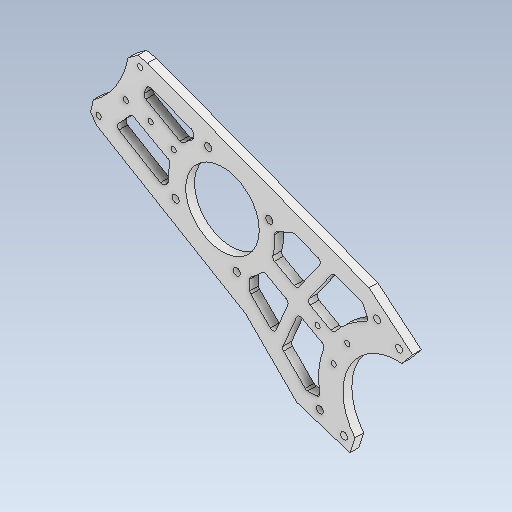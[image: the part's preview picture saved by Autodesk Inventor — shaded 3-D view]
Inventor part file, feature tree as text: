
AUTODESK INVENTOR PART (.ipt)
format: ipt  version: 2020 (Build 240168000, 168)  size: 496,128 bytes
history: native  units: mm
features: reference x14, sketch x11, extrude x10, other x7, thicken_offset x3, projected_geometry x3, chamfer x2, hole x1, fillet x1
ambient origin geometry x8: Origin, YZ Plane, XZ Plane, XY Plane, X Axis, Y Axis, Z Axis, Center Point
bodies: Solid1 (feature_tree)
feature tree (52):
  extrude  "Extrusion1"  Depth=5.0mm
  extrude  "Extrusion2"  Depth=5.0mm TaperAngle=0.0deg
  extrude  "Extrusion3"  Depth=4.0mm
  thicken_offset  "Thicken1"
  extrude  "Extrusion4"  Depth=5.0mm TaperAngle=0.0deg
  extrude  "Extrusion5"  Depth=10.0mm TaperAngle=0.0deg
  extrude  "Extrusion6"  Depth=2.0mm
  hole  "Hole1"  [1 undecoded]
  extrude  "Extrusion7"  Depth=10.0mm TaperAngle=0.0deg
  extrude  "Extrusion9"  Depth=60.0mm
  extrude  "Extrusion10"  Depth=10.0mm
  chamfer  "Chamfer1"  Angle=45.0deg  [1 undecoded]
  extrude  "Extrusion11"  TaperAngle=45.0deg  [1 undecoded]
  thicken_offset  "Thicken2"
  thicken_offset  "Thicken3"
  fillet  "Fillet4"  [1 undecoded]
  chamfer  "Chamfer2"  Angle=45.0deg  [1 undecoded]
  sketch  "Sketch1"  dims[d3=5.0mm d4=0.0mm d5=42.0mm]
  reference  "Reference1"
  reference  "Reference2"
  sketch  "Sketch2"  dims[d6=5.0mm d7=0.0mm d8=5.0mm d9=0.0mm]
  reference  "Reference3"
  sketch  "Sketch3"  dims[d10=4.0mm d11=4.0mm]
  reference  "Reference4"
  reference  "Reference5"
  sketch  "Sketch4"  dims[d13=40.0mm d14=5.0mm d15=0.0mm]
  projected_geometry  "Projected Loop1"
  sketch  "Sketch5"  dims[d16=10.0mm d17=0.0mm d18=10.0mm d19=0.0mm]
  reference  "Reference6"
  reference  "Reference7"
  reference  "Reference8"
  reference  "Reference9"
  sketch  "Sketch6"  dims[d20=3.0mm d21=6.0mm d22=4.0mm d23=2.0mm d24=90.0deg d25=8.0mm d26=0.0mm d27=28.0mm]
  projected_geometry  "Projected Loop2"
  sketch  "Sketch7"  dims[d28=18.675023mm d29=4.1mm]
  reference  "Reference10"
  reference  "Reference11"
  reference  "Reference12"
  reference  "Reference13"
  reference  "Reference14"
  sketch  "Sketch8"  dims[d30=40.0mm d32=360.0deg d34=10.0mm d35=0.0mm]
  sketch  "Sketch9"  dims[d36=90.0mm d37=60.0mm]
  sketch  "Sketch10"  dims[d38=14.0mm d39=10.0mm]
  projected_geometry  "Projected Loop3"
  sketch  "Sketch11"  dims[d40=10.0mm d43=45.0deg d44=45.0deg d45=45.0deg d46=45.0deg d47=10.0mm d48=0.0mm d49=62.0mm d50=120.0mm d51=14.0mm d52=10.0mm d53=10.0mm d54=10.0mm d55=0.0mm d56=5.0mm d57=2.0mm d58=45.0deg d59=3.0mm d60=3.0mm d61=3.0mm d62=5.0mm d63=0.0mm d67=2.0mm d68=2.0mm d69=2.0mm d70=2.0mm d71=2.0mm d72=5.0mm d73=2.0mm d74=45.0deg]
  parser-record x1  (decoder bookkeeping rows leaked as tree rows — omitted from the tree; the rows remain in map.json)
  other  "reducer_3.iam"
  other  "motor_h_3_m:1"
  other  "end_holder_1:1"
  other  "xl_wheel_ass:2"
  other  "xl_20_ori:1"
  other  "motor_h_4:1"
note: 5 required parameter values undecoded (feature->parameter linkage not recoverable at this tier; creation-order binding heuristic only, values carry confidence <= 0.55)
note: 1 file-system path scrubbed to <path> (originals preserved in map.json)
